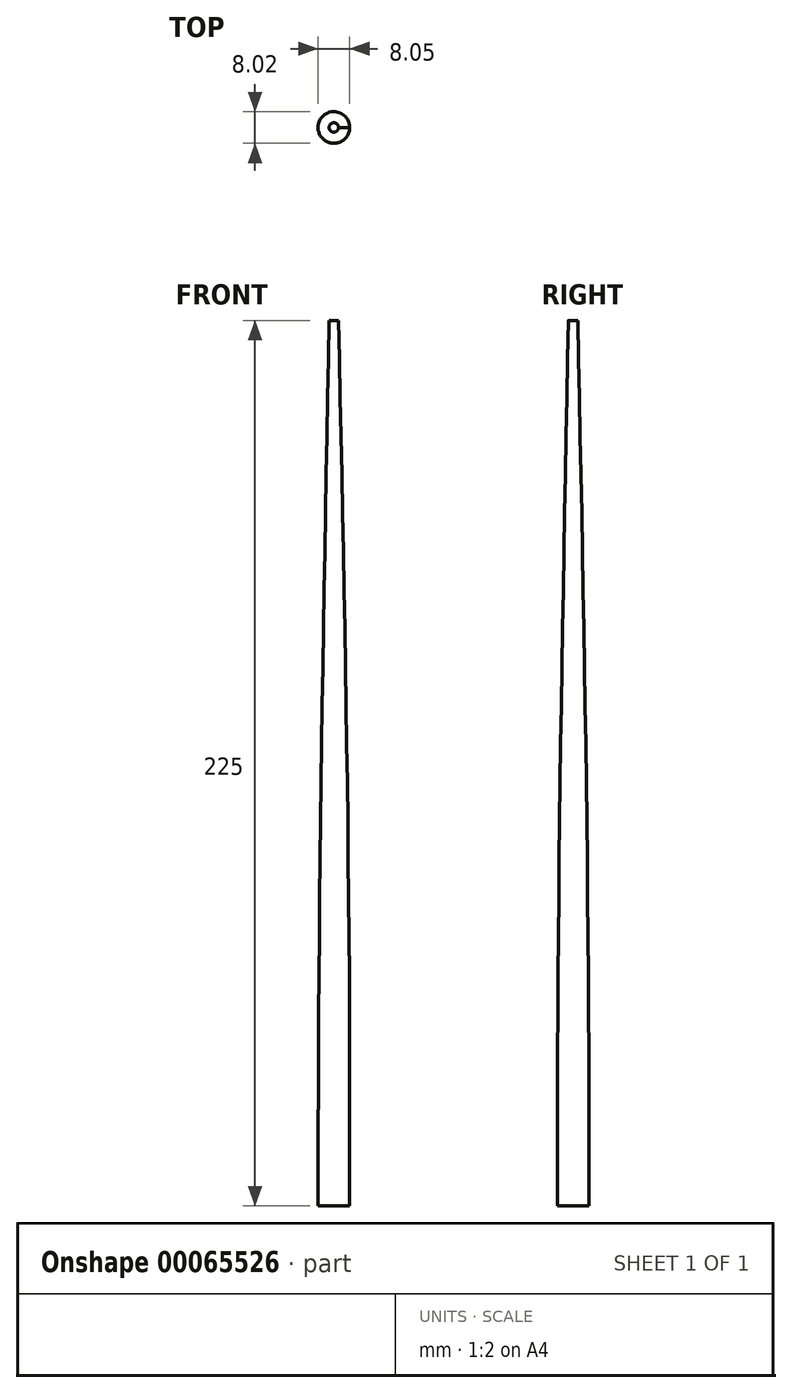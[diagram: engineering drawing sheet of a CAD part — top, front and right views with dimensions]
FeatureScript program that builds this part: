
annotation { "Feature Type Name" : "Feature", "Feature Type Description" : "" }
export const myFeature = defineFeature(function(context is Context, id is Id, definition is map)
    precondition{}
    {
        {
            var Q0;
            Q0=qCreatedBy(makeId("Top.planeOp"),FACE);
            var sketch = newSketch(context, id + "F0", { "sketchPlane" : qUnion([Q0])});
            skCircle(sketch, "E0", {"center": v(-32.2, 30.11) * mm, "radius": 4 * mm});
            skSolve(sketch);
        }
        {
            var Q0;
            Q0=qCreatedBy(makeId("Top.planeOp"),FACE);
            cPlane(context, id + "F1", {"entities" : qUnion([Q0]), "cplaneType" : CPlaneType.OFFSET, "offset" : 200 * mm, "width" : 150 * mm, "height" : 150 * mm});
        }
        {
            var Q0;
            Q0=qCreatedBy(makeId("Top.planeOp"),FACE);
            cPlane(context, id + "F2", {"entities" : qUnion([Q0]), "cplaneType" : CPlaneType.OFFSET, "offset" : 25 * mm, "oppositeDirection" : true, "width" : 150 * mm, "height" : 150 * mm});
        }
        {
            var Q0;
            Q0=qCreatedBy(id+"F2.planeOp",FACE);
            var sketch = newSketch(context, id + "F3", { "sketchPlane" : qUnion([Q0])});
            skCircle(sketch, "E1", {"center": v(-32.25, 30.1) * mm, "radius": 4 * mm});
            skSolve(sketch);
        }
        {
            var Q0;
            Q0=qCreatedBy(id+"F1.planeOp",FACE);
            var sketch = newSketch(context, id + "F4", { "sketchPlane" : qUnion([Q0])});
            skCircle(sketch, "E2", {"center": v(-32.23, 30.1) * mm, "radius": 1.2 * mm});
            skSolve(sketch);
        }
        {
            var Q0;
            Q0=makeQuery(id+"F4.imprint","IMPRINT",FACE,{"disambiguationData":[TD([[makeQuery(id+"F4.imprint","IMPRINT",EDGE,{"derivedFrom":sQuery(id+"F4.wireOp",EDGE,"E2")}),1.0]])]});
            var Q1;
            Q1=makeQuery(id+"F0.imprint","IMPRINT",FACE,{"disambiguationData":[TD([[makeQuery(id+"F0.imprint","IMPRINT",EDGE,{"derivedFrom":sQuery(id+"F0.wireOp",EDGE,"E0")}),1.0]])]});
            var Q2;
            Q2=makeQuery(id+"F3.imprint","IMPRINT",FACE,{"disambiguationData":[TD([[makeQuery(id+"F3.imprint","IMPRINT",EDGE,{"derivedFrom":sQuery(id+"F3.wireOp",EDGE,"E1")}),1.0]])]});
            loft(context, id + "F5", {"sheetProfilesArray" : [{ "sheetProfileEntities" : qUnion([Q0]) }, { "sheetProfileEntities" : qUnion([Q1]) }, { "sheetProfileEntities" : qUnion([Q2]) }]});
        }
    });
